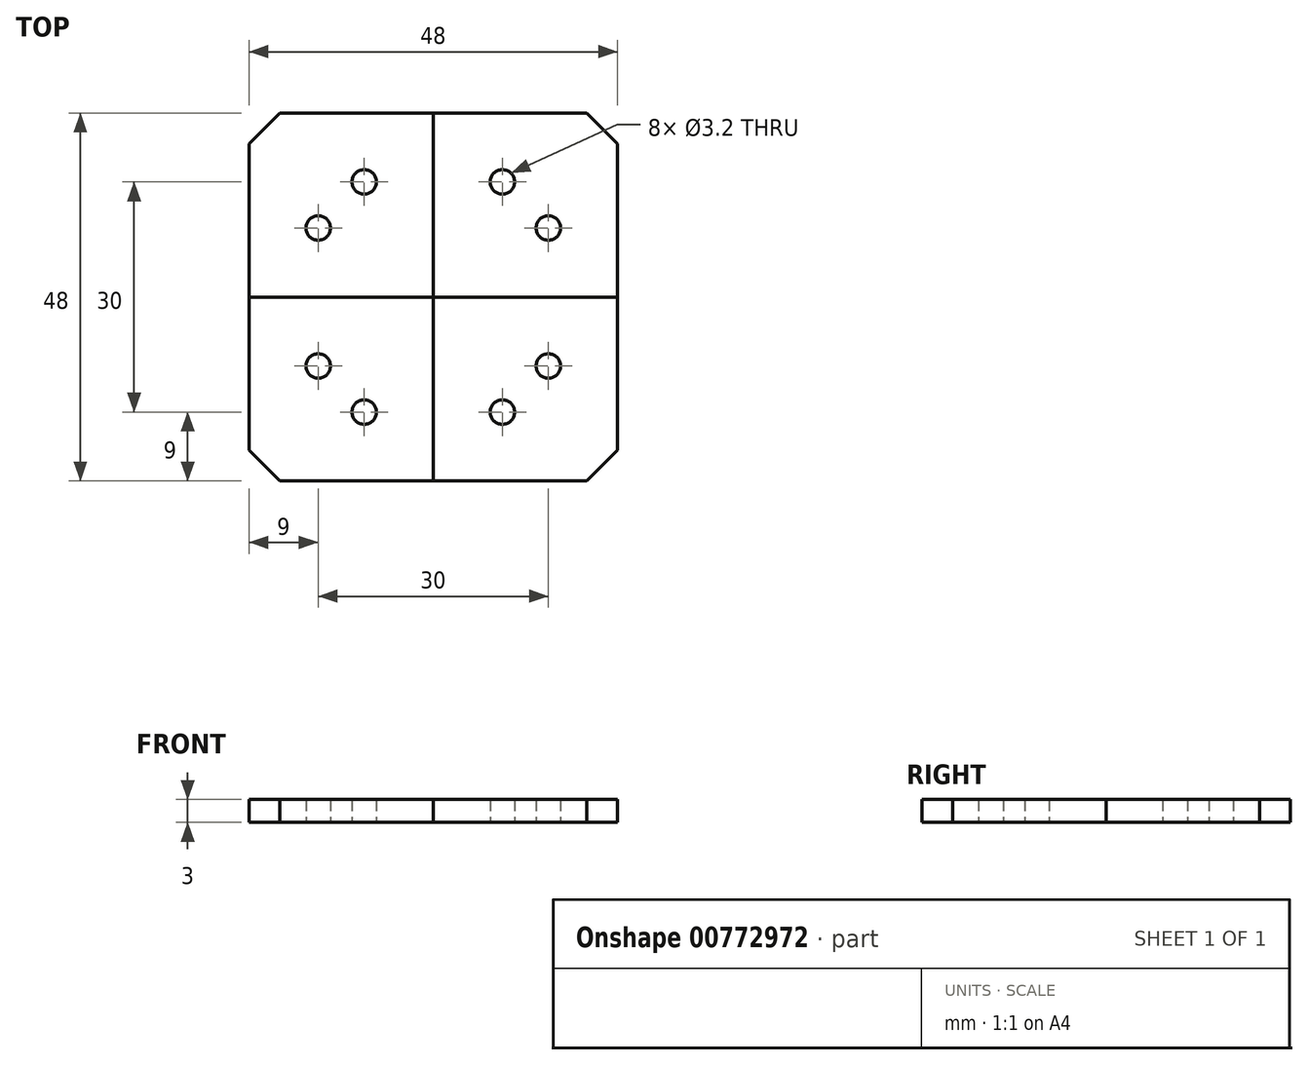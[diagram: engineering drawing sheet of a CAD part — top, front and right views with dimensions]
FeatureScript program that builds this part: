
annotation { "Feature Type Name" : "Feature", "Feature Type Description" : "" }
export const myFeature = defineFeature(function(context is Context, id is Id, definition is map)
    precondition{}
    {
        {
            var Q0;
            Q0=qCreatedBy(makeId("Top.planeOp"),FACE);
            var sketch = newSketch(context, id + "F0", { "sketchPlane" : qUnion([Q0])});
            skLineSegment(sketch, "E0.bottom", {"start": v(0, 0) * mm, "end": v(25, 0) * mm});
            skLineSegment(sketch, "E0.top", {"start": v(0, 25) * mm, "end": v(25, 25) * mm});
            skLineSegment(sketch, "E0.left", {"start": v(0, 0) * mm, "end": v(0, 25) * mm});
            skLineSegment(sketch, "E0.right", {"start": v(25, 0) * mm, "end": v(25, 25) * mm});
            skCircle(sketch, "E1", {"center": v(10, 16) * mm, "radius": 1.6 * mm});
            skCircle(sketch, "E2", {"center": v(16, 10) * mm, "radius": 1.6 * mm});
            skLineSegment(sketch, "E3", {"start": v(1, 25) * mm, "end": v(1, 0) * mm});
            skLineSegment(sketch, "E4", {"start": v(0, 1) * mm, "end": v(25, 1) * mm});
            skSolve(sketch);
        }
        {
            var Q0;
            Q0=makeQuery(id+"F0.imprint","IMPRINT",FACE,{"disambiguationData":[TD([[makeQuery(id+"F0.imprint","IMPRINT",EDGE,{"derivedFrom":sQuery(id+"F0.wireOp",EDGE,"E1")}),-1.0]])]});
            extrude(context, id + "F1", {"entities" : qUnion([Q0]), "depth" : 3 * mm, "offsetDistance" : 25 * mm});
        }
        {
            var Q0;
            Q0=makeQuery(id+"F1.opExtrude","SWEPT_EDGE",EDGE,{"disambiguationData":[OSD([sQuery(id+"F0.wireOp",EDGE,"E3"),sQuery(id+"F0.wireOp",EDGE,"E4")])]});
            chamfer(context, id + "F2", {"entities" : qUnion([Q0]), "width" : 4 * mm, "tangentPropagation" : true});
        }
        {
            var Q0;
            Q0=makeQuery(id+"F1.opExtrude","SWEPT_BODY",BODY,{"disambiguationData":[OSD([sQuery(id+"F0.wireOp",EDGE,"E0.top"),sQuery(id+"F0.wireOp",EDGE,"E0.right"),sQuery(id+"F0.wireOp",EDGE,"E1"),sQuery(id+"F0.wireOp",EDGE,"E2"),sQuery(id+"F0.wireOp",EDGE,"E3"),sQuery(id+"F0.wireOp",EDGE,"E4")])]});
            var Q1;
            Q1=makeQuery(id+"F1.opExtrude","SWEPT_EDGE",EDGE,{"disambiguationData":[OSD([sQuery(id+"F0.wireOp",EDGE,"E0.top"),sQuery(id+"F0.wireOp",EDGE,"E0.right")])]});
            circularPattern(context, id + "F3", {"entities" : qUnion([Q0]), "axis" : qUnion([Q1]), "angle" : 360 * degree, "instanceCount" : 4, "equalSpace" : true});
        }
    });
